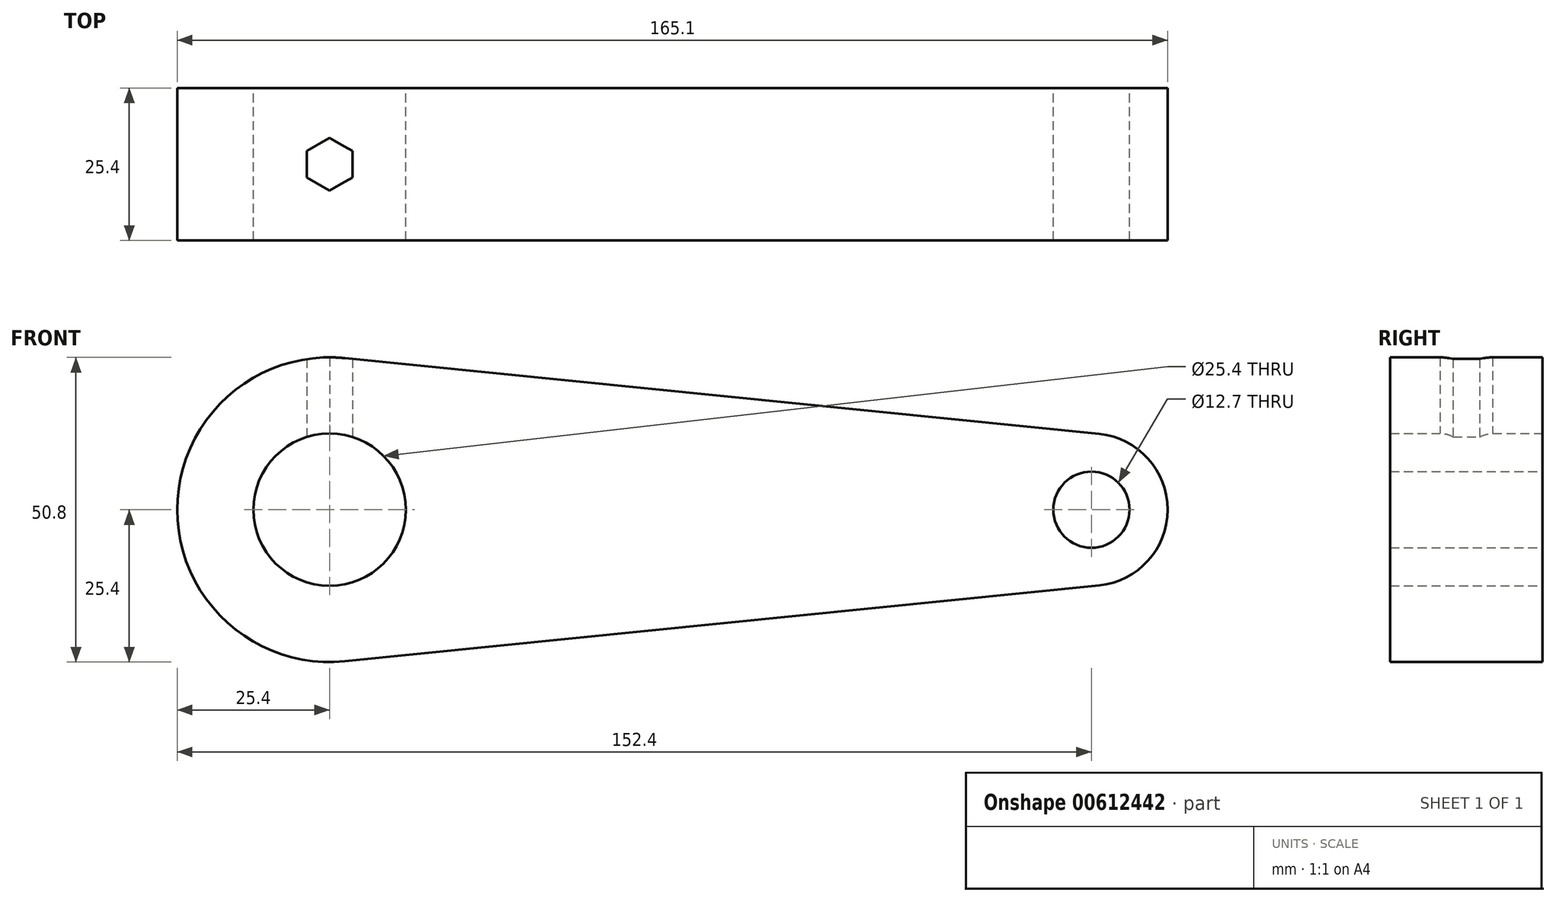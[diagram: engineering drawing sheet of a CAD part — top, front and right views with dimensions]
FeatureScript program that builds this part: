
annotation { "Feature Type Name" : "Feature", "Feature Type Description" : "" }
export const myFeature = defineFeature(function(context is Context, id is Id, definition is map)
    precondition{}
    {
        {
            var Q0;
            Q0=qCreatedBy(makeId("Front.planeOp"),FACE);
            var sketch = newSketch(context, id + "F0", { "sketchPlane" : qUnion([Q0])});
            skCircle(sketch, "E0", {"center": v(0, 0) * mm, "radius": 25.4 * mm});
            skCircle(sketch, "E1", {"center": v(127, 0) * mm, "radius": 12.7 * mm});
            skCircle(sketch, "E2", {"center": v(0, 0) * mm, "radius": 12.7 * mm});
            skCircle(sketch, "E3", {"center": v(127, 0) * mm, "radius": 6.35 * mm});
            skLineSegment(sketch, "E4", {"start": v(2.54, 25.27) * mm, "end": v(128.27, 12.64) * mm});
            skLineSegment(sketch, "E5", {"start": v(2.54, -25.27) * mm, "end": v(128.27, -12.64) * mm});
            skSolve(sketch);
        }
        {
            var Q0;
            Q0 = qSketchRegion(id + "F0", true);
            extrude(context, id + "F1", {"entities" : qUnion([Q0]), "depth" : 25.4 * mm, "offsetDistance" : 25.4 * mm});
        }
        {
            var Q0;
            Q0=qCreatedBy(makeId("Top.planeOp"),FACE);
            var sketch = newSketch(context, id + "F2", { "sketchPlane" : qUnion([Q0])});
            skLineSegment(sketch, "E6", {"start": v(0, 0) * mm, "end": v(0, -25.4) * mm});
            skCircle(sketch, "E7", {"center": v(0, -12.7) * mm, "radius": 3.81 * mm});
            skCircle(sketch, "E8.cCircle", {"center": v(0, -12.7) * mm, "radius": 3.81 * mm, "construction": true});
            skLineSegment(sketch, "E8.0", {"start": v(3.81, -10.5) * mm, "end": v(3.81, -14.9) * mm});
            skLineSegment(sketch, "E8.1", {"start": v(3.81, -14.9) * mm, "end": v(0, -17.1) * mm});
            skLineSegment(sketch, "E8.2", {"start": v(0, -17.1) * mm, "end": v(-3.8, -14.9) * mm});
            skLineSegment(sketch, "E8.3", {"start": v(-3.8, -14.9) * mm, "end": v(-3.81, -10.5) * mm});
            skLineSegment(sketch, "E8.4", {"start": v(-3.81, -10.5) * mm, "end": v(0, -8.3) * mm});
            skLineSegment(sketch, "E8.5", {"start": v(0, -8.3) * mm, "end": v(3.81, -10.5) * mm});
            skPoint(sketch, "E8.0.midPoint", {"position": v(3.81, -12.7) * mm});
            skSolve(sketch);
        }
        {
            var Q0;
            Q0 = qSketchRegion(id + "F2", true);
            extrude(context, id + "F3", {"entities" : qUnion([Q0]), "operationType" : NewBodyOperationType.REMOVE, "depth" : 36.58 * mm, "offsetDistance" : 25.4 * mm});
        }
    });
